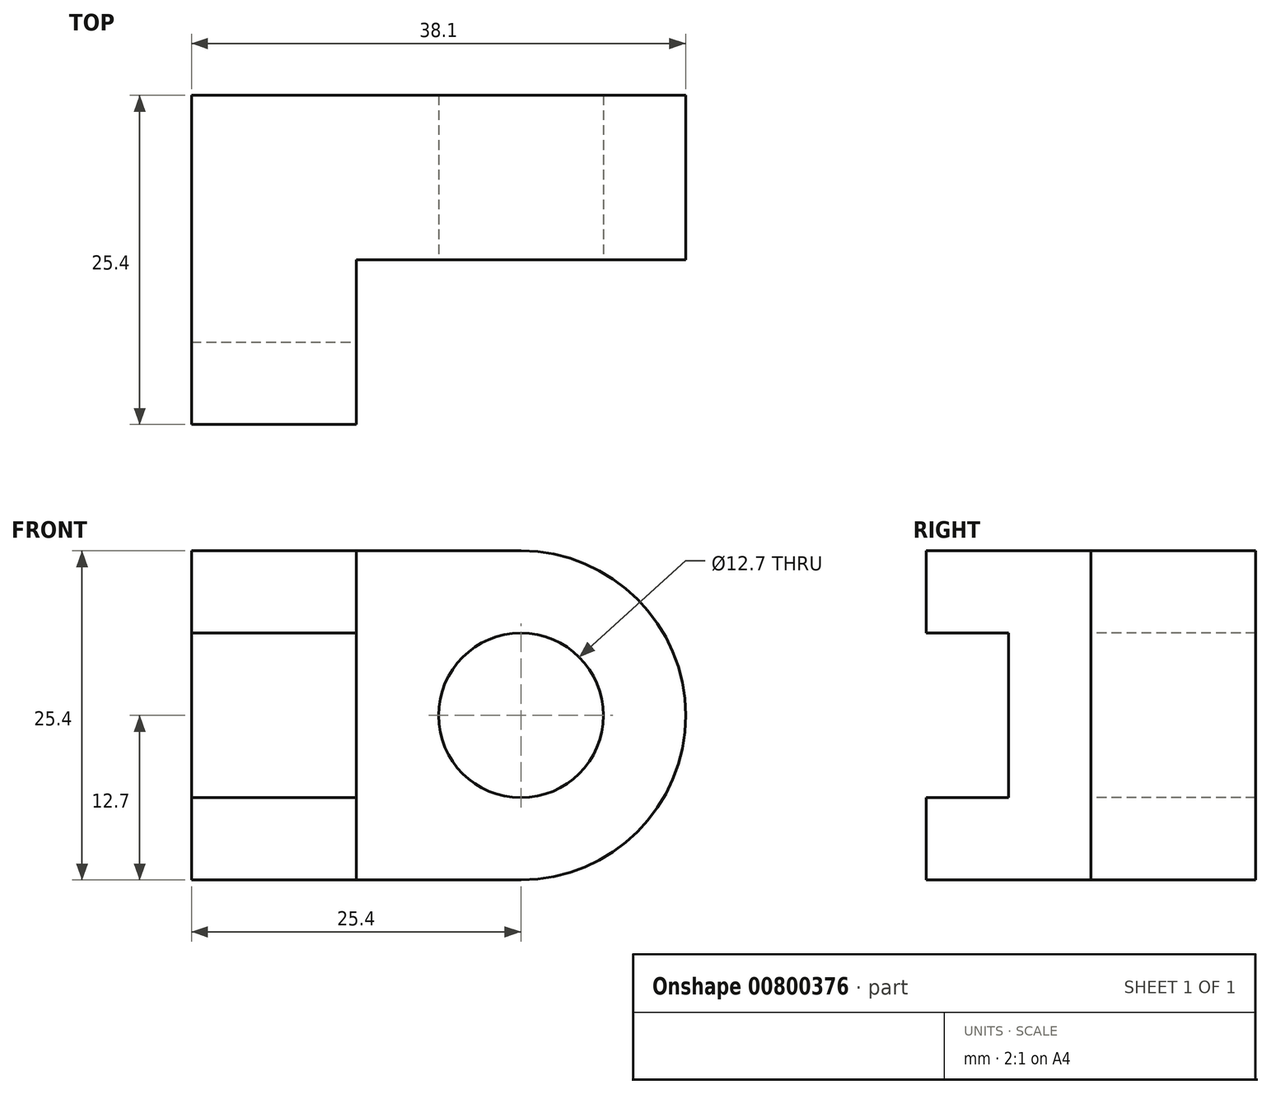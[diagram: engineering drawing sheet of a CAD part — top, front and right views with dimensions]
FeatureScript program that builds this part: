
annotation { "Feature Type Name" : "Feature", "Feature Type Description" : "" }
export const myFeature = defineFeature(function(context is Context, id is Id, definition is map)
    precondition{}
    {
        {
            var Q0;
            Q0=qCreatedBy(makeId("Top.planeOp"),FACE);
            var sketch = newSketch(context, id + "F0", { "sketchPlane" : qUnion([Q0])});
            skLineSegment(sketch, "E0", {"start": v(0, 0) * mm, "end": v(0, -25.4) * mm});
            skLineSegment(sketch, "E1", {"start": v(0, -25.4) * mm, "end": v(12.7, -25.4) * mm});
            skLineSegment(sketch, "E2", {"start": v(12.7, -25.4) * mm, "end": v(12.7, -12.7) * mm});
            skLineSegment(sketch, "E3", {"start": v(12.7, -12.7) * mm, "end": v(76.2, -12.7) * mm});
            skLineSegment(sketch, "E4", {"start": v(76.2, -12.7) * mm, "end": v(76.2, 0) * mm});
            skLineSegment(sketch, "E5", {"start": v(76.2, 0) * mm, "end": v(0, 0) * mm});
            skSolve(sketch);
        }
        {
            var Q0;
            Q0 = qSketchRegion(id + "F0", true);
            extrude(context, id + "F1", {"entities" : qUnion([Q0]), "depth" : 25.4 * mm, "offsetDistance" : 25.4 * mm});
        }
        {
            var Q0;
            Q0=makeQuery(id+"F1.opExtrude","SWEPT_FACE",FACE,{"disambiguationData":[OSD([sQuery(id+"F0.wireOp",EDGE,"E2")])]});
            var sketch = newSketch(context, id + "F2", { "sketchPlane" : qUnion([Q0])});
            skLineSegment(sketch, "E6", {"start": v(-25.4, 25.4) * mm, "end": v(-25.4, 19.05) * mm});
            skLineSegment(sketch, "E7", {"start": v(-25.4, 19.05) * mm, "end": v(-19.05, 19.05) * mm});
            skLineSegment(sketch, "E8", {"start": v(-19.05, 19.05) * mm, "end": v(-19.05, 6.35) * mm});
            skLineSegment(sketch, "E9", {"start": v(-19.05, 6.35) * mm, "end": v(-25.4, 6.35) * mm});
            skLineSegment(sketch, "E10", {"start": v(-25.4, 6.35) * mm, "end": v(-25.4, 0) * mm});
            skSolve(sketch);
        }
        {
            var Q0;
            {var subQ0=sQuery(id+"F2.wireOp",EDGE,"E7");Q0=makeQuery(id+"F2.imprint","IMPRINT",FACE,{"disambiguationData":[TD([[makeQuery(id+"F2.imprint","IMPRINT",EDGE,{"derivedFrom":subQ0}),-1.0]])]});}
            extrude(context, id + "F3", {"entities" : qUnion([Q0]), "operationType" : NewBodyOperationType.REMOVE, "oppositeDirection" : true, "depth" : 12.7 * mm, "offsetDistance" : 25.4 * mm});
        }
        {
            var Q0;
            Q0=makeQuery(id+"F1.opExtrude","SWEPT_FACE",FACE,{"disambiguationData":[OSD([sQuery(id+"F0.wireOp",EDGE,"E3")])]});
            var sketch = newSketch(context, id + "F4", { "sketchPlane" : qUnion([Q0])});
            skLineSegment(sketch, "E11", {"start": v(12.7, 25.4) * mm, "end": v(25.4, 25.4) * mm});
            skLineSegment(sketch, "E12", {"start": v(12.7, 0) * mm, "end": v(25.4, 0) * mm});
            skArc(sketch, "E13", {"start": v(25.4, 0) * mm, "mid": v(38.1, 12.7) * mm, "end": v(25.4, 25.4) * mm});
            skSolve(sketch);
        }
        {
            var Q0;
            {var subQ0=sQuery(id+"F4.wireOp",EDGE,"E13");Q0=makeQuery(id+"F4.imprint","IMPRINT",FACE,{"disambiguationData":[TD([[makeQuery(id+"F4.imprint","IMPRINT",EDGE,{"derivedFrom":subQ0}),-1.0]])]});}
            extrude(context, id + "F5", {"entities" : qUnion([Q0]), "operationType" : NewBodyOperationType.REMOVE, "oppositeDirection" : true, "depth" : 12.7 * mm, "offsetDistance" : 25.4 * mm});
        }
        {
            var Q0;
            Q0=makeQuery(id+"F1.opExtrude","SWEPT_FACE",FACE,{"disambiguationData":[OSD([sQuery(id+"F0.wireOp",EDGE,"E3")])]});
            var sketch = newSketch(context, id + "F6", { "sketchPlane" : qUnion([Q0])});
            skLineSegment(sketch, "E14", {"start": v(25.4, 25.4) * mm, "end": v(25.4, 12.7) * mm, "construction": true});
            skCircle(sketch, "E15", {"center": v(25.4, 12.7) * mm, "radius": 6.35 * mm});
            skSolve(sketch);
        }
        {
            var Q0;
            Q0=makeQuery(id+"F6.imprint","IMPRINT",FACE,{"disambiguationData":[TD([[makeQuery(id+"F6.imprint","IMPRINT",EDGE,{"derivedFrom":sQuery(id+"F6.wireOp",EDGE,"E15")}),1.0]])]});
            extrude(context, id + "F7", {"entities" : qUnion([Q0]), "operationType" : NewBodyOperationType.REMOVE, "oppositeDirection" : true, "depth" : 12.7 * mm, "offsetDistance" : 25.4 * mm});
        }
    });
